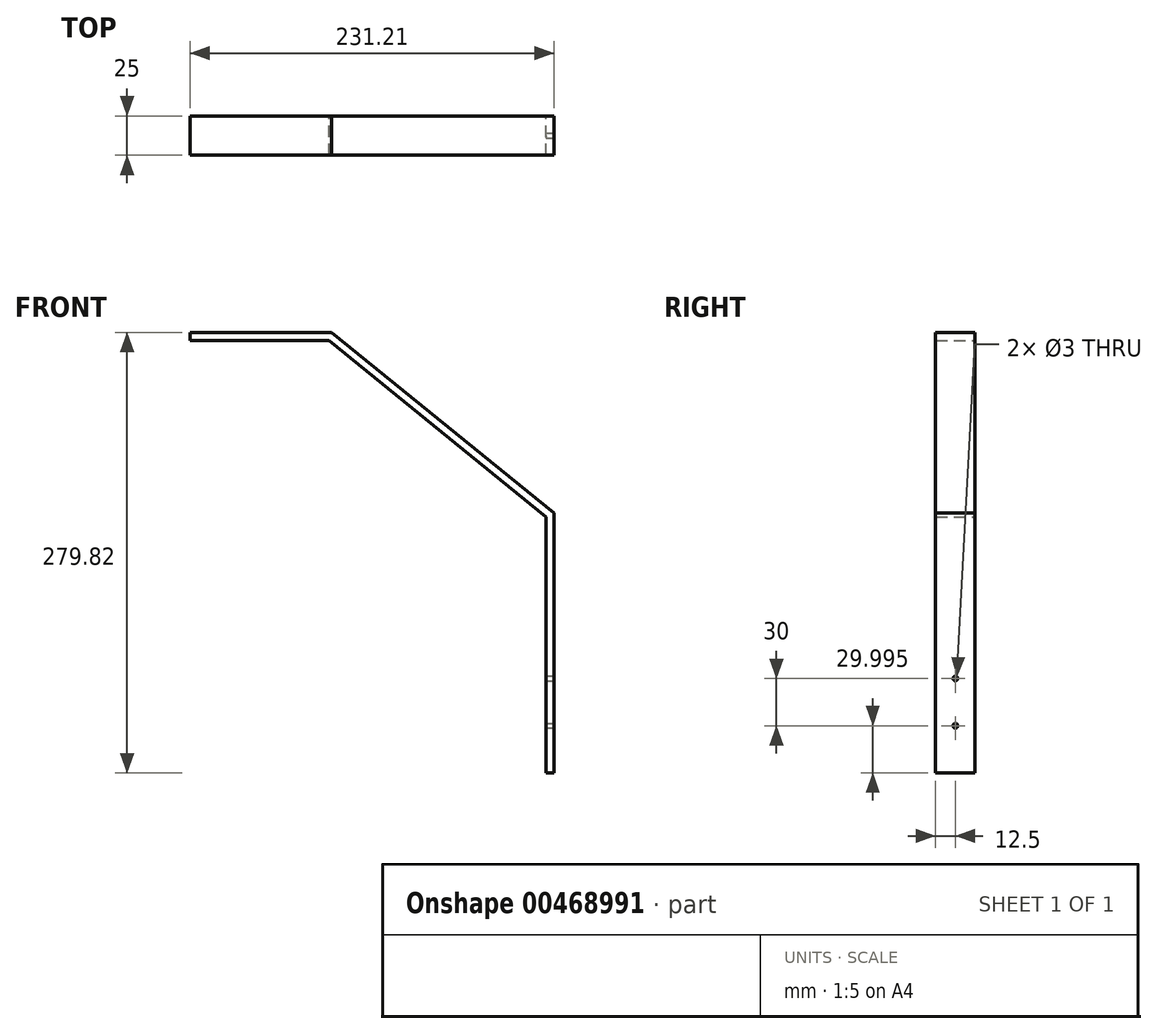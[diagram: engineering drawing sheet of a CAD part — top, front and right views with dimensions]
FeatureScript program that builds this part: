
annotation { "Feature Type Name" : "Feature", "Feature Type Description" : "" }
export const myFeature = defineFeature(function(context is Context, id is Id, definition is map)
    precondition{}
    {
        {
            var Q0;
            Q0=qCreatedBy(makeId("Front.planeOp"),FACE);
            var sketch = newSketch(context, id + "F0", { "sketchPlane" : qUnion([Q0])});
            skLineSegment(sketch, "E0.top", {"start": v(3.71, 270) * mm, "end": v(91.93, 270) * mm});
            skLineSegment(sketch, "E0.right", {"start": v(229.92, 0.07) * mm, "end": v(229.92, 157.8) * mm});
            skLineSegment(sketch, "E1", {"start": v(229.92, 157.8) * mm, "end": v(91.93, 270) * mm});
            skLineSegment(sketch, "E2.0", {"start": v(234.92, 160.18) * mm, "end": v(93.71, 275) * mm});
            skLineSegment(sketch, "E2.1", {"start": v(3.71, 275) * mm, "end": v(93.71, 275) * mm});
            skLineSegment(sketch, "E2.2", {"start": v(234.92, -4.82) * mm, "end": v(234.92, 160.18) * mm});
            skLineSegment(sketch, "E2.3", {"start": v(229.92, -4.82) * mm, "end": v(234.92, -4.82) * mm});
            skLineSegment(sketch, "E3", {"start": v(3.71, 270) * mm, "end": v(3.71, 275) * mm});
            skLineSegment(sketch, "E4", {"start": v(229.92, 0.07) * mm, "end": v(229.92, -4.82) * mm});
            skSolve(sketch);
        }
        {
            var Q0;
            Q0 = qSketchRegion(id + "F0", true);
            extrude(context, id + "F1", {"entities" : qUnion([Q0]), "depth" : 25 * mm});
        }
        {
            var Q0;
            Q0=makeQuery(id+"F1.opExtrude","SWEPT_FACE",FACE,{"disambiguationData":[OSD([sQuery(id+"F0.wireOp",EDGE,"E2.2")])]});
            var sketch = newSketch(context, id + "F2", { "sketchPlane" : qUnion([Q0])});
            skCircle(sketch, "E5", {"center": v(-12.5, 25.18) * mm, "radius": 1.5 * mm});
            skPoint(sketch, "E5.centerSnap0", {"position": v(-12.5, -4.82) * mm});
            skCircle(sketch, "E6", {"center": v(-12.5, 55.18) * mm, "radius": 1.5 * mm});
            skSolve(sketch);
        }
        {
            var Q0;
            Q0 = qSketchRegion(id + "F2", true);
            extrude(context, id + "F3", {"entities" : qUnion([Q0]), "operationType" : NewBodyOperationType.REMOVE, "endBound" : BoundingType.THROUGH_ALL, "oppositeDirection" : true, "depth" : 25 * mm});
        }
    });
